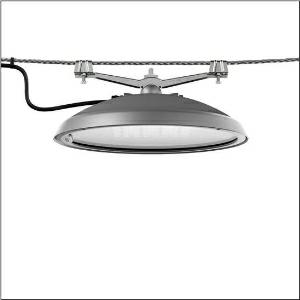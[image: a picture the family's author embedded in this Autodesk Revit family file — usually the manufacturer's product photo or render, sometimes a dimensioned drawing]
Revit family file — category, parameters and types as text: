
# Revit family: dl_50_iq_mini___st1_0s_5xa248w21f08re_36e9
name_source: partatom
category: Lighting Fixtures
units: mm (PartAtom-declared; Revit-internal decimal feet)

## family parameters
Cut with Voids When Loaded = No
Host = Face
Light Source = No
Part Type = Normal
Room Calculation Point = No
Round Connector Dimension = Use Diameter
Shared = No

## types (1)
- --- (1 x LED, 5120 lm, 36.6 W, 2200K)
    Apparent Load = 37 VA
    CIE Flux Codes = 37 72 97 100 100
    Color Rendering = 70
    Color Temperature = 2200K
    Default Elevation = 1800 mm
    Description = DL 50 iQ mini, catenary luminaire, primary light control with lens, of PMMA, primary optical cover: cover, of toughened safety glass, transparent, light distribution: ST1.0s, light emission: direct distribution, primary light characteristic: symmetric, installation type: suspended mounting, LED, High Power LED, rated luminous flux: 5.120lm, luminous efficacy: 140lm/W, light colour: 722, colour temperature: 2200K, control gear: iQ Street-Remote, control: optimised constant luminous flux control (CLO 2.0), Desk-Remote (wireless, voltage-free reading and setting of iQ features in the workshop via application-optimized NFC function/RFID function), Light-Fading, Smart-Wire, Night-Set, Lumen-Switch, Temp-Guard, Auto-Match, Street-Remote, mains connection: 230..240V, AC, 50/60Hz, start of lifetime: 37W, end of service life: 38W, reduction: 18W, luminaire housing, of diecast aluminium, powder-coated, SITECO metallic grey (DB 702S), diameter: 500mm, height: 115mm, mounting height: 4..12m, protection rating (complete): IP66, insulation class (complete): insulation class II (safety insulation), certification: CE, ENEC, ENEC+, VDE, impact resistance: IK08, permissible operating ambient temperature for outdoor applications: -25..+40°C, standard-compliant lighting for roads and squares, packaging unit: 1 piece

Light Distribution: ST1.0s
    Height = 124 mm  [stored 0.406824 ft]
    Lamp = 1 x LED
    Lamp Light Flux = 5120 lm
    Lamp Power = 36.6 W
    Lamp count = 1
    Length = 500 mm
    Luminous efficacy = 140 lm/W
    Manufacturer = Siteco
    ModVariant = No
    Model = 5XA248W21F08RE
    Number of Poles = 1
    OnlyDefault = Yes
    Power Factor = 1
    Product Name = DL 50 iQ mini | ST1.0s
    Product group = catenary luminaire
    ProductGroupID = 6300
    Protection Class = Protection class II
    Protection Degree = IP 66
    RLX_Detail_Level = 1
    RLX_Emergency_Light_Flux = 0 lm
    RLX_Emergency_Type = 0
    RLX_Emergency_Type_DB = No
    RlxData = <blob elided: 123649 chars, md5=f6e7dcb5>
    Socket = socket
    Standby Power = 0 W
    System Light Flux = 5120 lm
    System Power = 37 W
    Type Comments = factory setting: luminous flux: 100 % | dim-lin: 254 | 388 mA
    Type Image = l_1242791.jpg
    URL = http://relux.com
    VarID = @adj_140287
    Voltage = 0 V
    Weight = 0.00 kg
    Width = 0 mm  [stored 0 ft]

note: [stored X ft] marks values corroborated as IEEE doubles in the binary element streams (Revit-internal decimal feet)

## geometry (parser evidence)
native form markers: Blend x4, Sweep x10
no freeform markers — native parametric forms only
